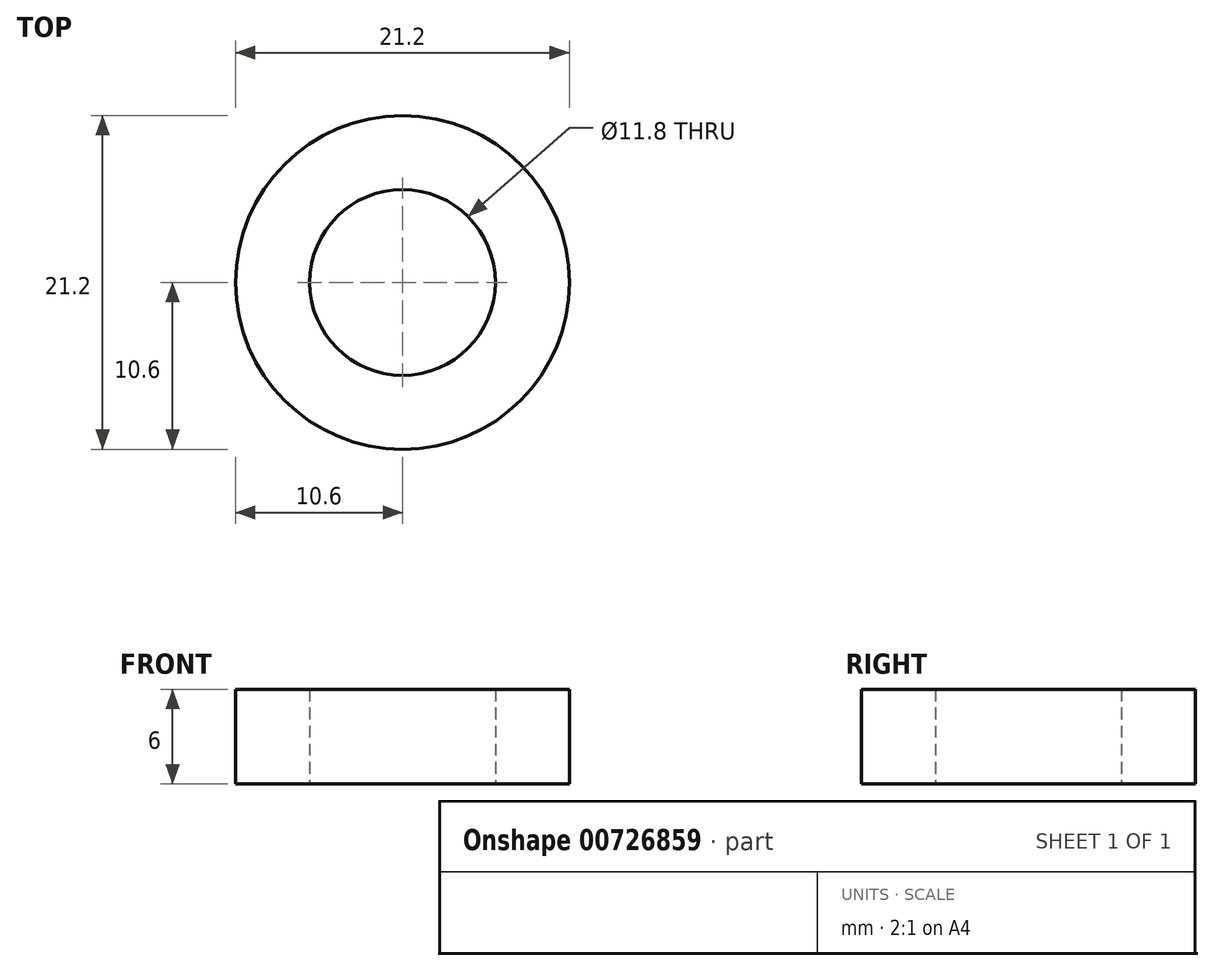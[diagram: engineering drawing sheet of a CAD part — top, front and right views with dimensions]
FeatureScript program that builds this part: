
annotation { "Feature Type Name" : "Feature", "Feature Type Description" : "" }
export const myFeature = defineFeature(function(context is Context, id is Id, definition is map)
    precondition{}
    {
        {
            var Q0;
            Q0=qCreatedBy(makeId("Top.planeOp"),FACE);
            var sketch = newSketch(context, id + "F0", { "sketchPlane" : qUnion([Q0])});
            skCircle(sketch, "E0", {"center": v(0, 0) * mm, "radius": 10.6 * mm});
            skCircle(sketch, "E1", {"center": v(0, 0) * mm, "radius": 5.9 * mm});
            skSolve(sketch);
        }
        {
            var Q0;
            Q0=makeQuery(id+"F0.imprint","IMPRINT",FACE,{"disambiguationData":[TD([[makeQuery(id+"F0.imprint","IMPRINT",EDGE,{"derivedFrom":sQuery(id+"F0.wireOp",EDGE,"E0")}),1.0]])]});
            extrude(context, id + "F1", {"entities" : qUnion([Q0]), "depth" : 6 * mm, "offsetDistance" : 25 * mm});
        }
    });
